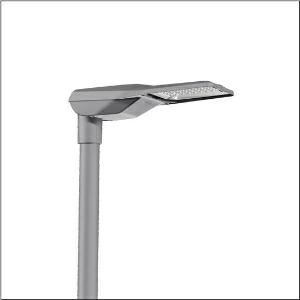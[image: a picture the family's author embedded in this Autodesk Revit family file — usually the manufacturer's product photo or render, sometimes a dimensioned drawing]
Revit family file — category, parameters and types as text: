
# Revit family: streetlight_sl_21_iq_mini___stw1_0a_5xe2e31g08hb_9864
name_source: partatom
category: Lighting Fixtures
units: mm (PartAtom-declared; Revit-internal decimal feet)

## family parameters
Cut with Voids When Loaded = No
Host = Face
Light Source = No
Part Type = Normal
Room Calculation Point = No
Round Connector Dimension = Use Diameter
Shared = No

## types (1)
- --- (1 x LED, 9450 lm, 70.9 W, 3000K)
    Apparent Load = 71 VA
    CIE Flux Codes = 38 75 98 100 100
    Color Rendering = 70
    Color Temperature = 3000K
    Default Elevation = 1800 mm
    Description = Streetlight SL 21 iQ mini, mast luminaire, primary light control with lens, of PMMA, primary optical cover: cover, of toughened safety glass, transparent, light distribution: STW1.0a, light emission: direct distribution, primary light characteristic: asymmetric, installation type: post-top, side-entry, LED, High Power LED, rated luminous flux: 9.450lm, luminous efficacy: 133lm/W, light colour: 730, colour temperature: 3000K, control: Street-Remote, Auto-Match, Temp-Guard, Lumen-Switch, Night-Set, Smart-Wire, Light-Fading, Desk-Remote (wireless, voltage-free reading and setting of iQ features in the workshop via application-optimized NFC function/RFID function), optimised constant luminous flux control (CLO 2.0), presetting dimming linear, mains connection: 220..240V, AC, 50/60Hz, start of lifetime: 71W, end of service life: 75W, reduction: 31W, luminaire housing, of diecast aluminium, powder-coated, Siteco® metallic grey (DB 702S), corrosivity category C5 mid according to DIN EN ISO 12944, please order mast flange separately, inclination adjustable: 0°, 5°, 10°, 15°, sealing non-destructively replaceable, multi-level sealing system, length: 628mm, width: 235mm, height: 110mm, mast flange for spigot size: 42mm (side-entry): 5XC10008XM4, 60/48mm (side-entry/post-top): 5XC10108XM2, 76/60mm (side-entry/post-top): 5XC10108XM1, protection rating (complete): IP66, insulation class (complete): insulation class II (safety insulation), certification: CE, ENEC, ENEC+, VDE, impact resistance: IK09, permissible operating ambient temperature for outdoor applications: -40..+50°C, standard-compliant lighting for roads and squares, packaging unit: 1 piece

Light Distribution: STW1.0a
    Height = 110 mm
    Lamp = 1 x LED
    Lamp Light Flux = 9450 lm
    Lamp Power = 70.9 W
    Lamp count = 1
    Length = 625 mm
    Luminous efficacy = 133 lm/W
    Manufacturer = Siteco
    ModVariant = No
    Model = 5XE2E31G08HB
    Number of Poles = 1
    OnlyDefault = Yes
    Power Factor = 1
    Product Name = Streetlight SL 21 iQ mini | STW1.0a
    Product group = mast luminaire | pylon top
    ProductGroupID = 6100
    Protection Class = Protection class II
    Protection Degree = IP 66
    RLX_Detail_Level = 1
    RLX_Emergency_Light_Flux = 0 lm
    RLX_Emergency_Type = 0
    RLX_Emergency_Type_DB = No
    RlxData = <blob elided: 92005 chars, md5=070509a0>
    Socket = socket
    Standby Power = 0 W
    System Light Flux = 9450 lm
    System Power = 71 W
    Type Comments = factory setting: luminous flux: 100 % | dim-lin: 254 | 711 mA
    Type Image = l_1003519.jpg
    URL = http://relux.com
    VarID = @adj_090153
    Voltage = 0 V
    Weight = 0.00 kg
    Width = 234 mm

## geometry (parser evidence)
native form markers: Blend x4, Sweep x11
no freeform markers — native parametric forms only
